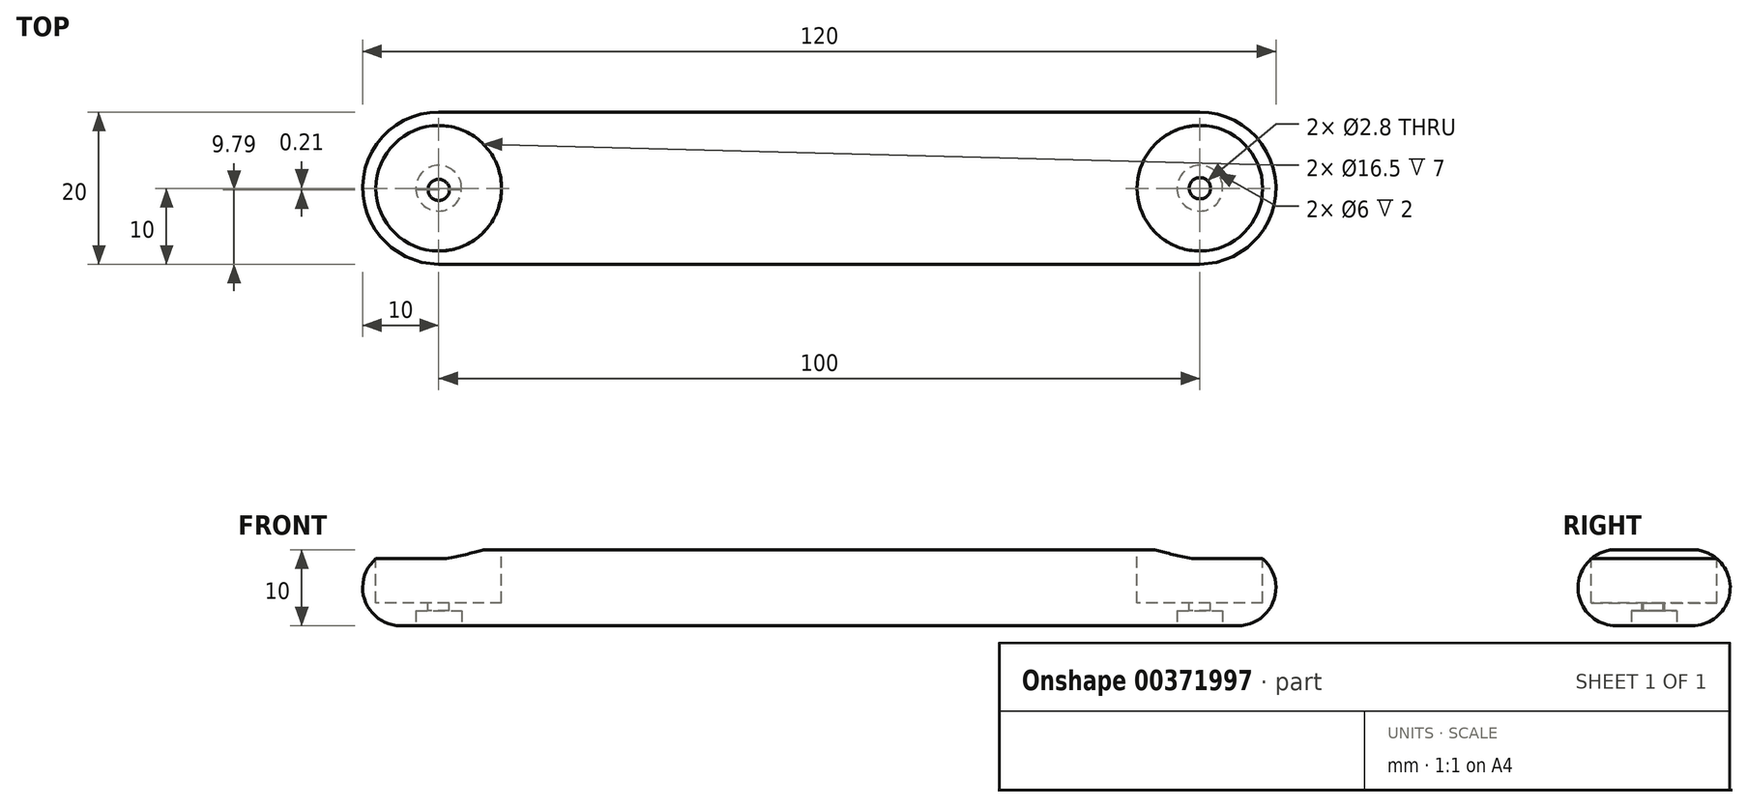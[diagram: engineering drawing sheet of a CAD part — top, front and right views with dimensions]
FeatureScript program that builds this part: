
annotation { "Feature Type Name" : "Feature", "Feature Type Description" : "" }
export const myFeature = defineFeature(function(context is Context, id is Id, definition is map)
    precondition{}
    {
        {
            var Q0;
            Q0=qCreatedBy(makeId("Top.planeOp"),FACE);
            var sketch = newSketch(context, id + "F0", { "sketchPlane" : qUnion([Q0])});
            skArc(sketch, "E0", {"start": v(0, 10) * mm, "mid": v(-10, 0) * mm, "end": v(0, -10) * mm});
            skArc(sketch, "E1", {"start": v(100, -10) * mm, "mid": v(110, 0) * mm, "end": v(100, 10) * mm});
            skLineSegment(sketch, "E2", {"start": v(0, 10) * mm, "end": v(100, 10) * mm});
            skLineSegment(sketch, "E3", {"start": v(0, -10) * mm, "end": v(100, -10) * mm});
            skSolve(sketch);
        }
        {
            var Q0;
            Q0=makeQuery(id+"F0.imprint","IMPRINT",FACE,{"disambiguationData":[TD([[makeQuery(id+"F0.imprint","IMPRINT",EDGE,{"derivedFrom":sQuery(id+"F0.wireOp",EDGE,"E0")}),1.0]])]});
            extrude(context, id + "F1", {"entities" : qUnion([Q0]), "depth" : 10 * mm});
        }
        {
            var Q0;
            Q0=makeQuery(id+"F1.opExtrude","CAP_FACE",FACE,{"disambiguationData":[OSD([sQuery(id+"F0.wireOp",EDGE,"E0"),sQuery(id+"F0.wireOp",EDGE,"E1"),sQuery(id+"F0.wireOp",EDGE,"E2"),sQuery(id+"F0.wireOp",EDGE,"E3")])],"isStart":false});
            var sketch = newSketch(context, id + "F2", { "sketchPlane" : qUnion([Q0])});
            skLineSegment(sketch, "E4.0.0", {"start": v(0, -10) * mm, "end": v(100, -10) * mm});
            skArc(sketch, "E4.0.1", {"start": v(100, -10) * mm, "mid": v(110, 0) * mm, "end": v(100, 10) * mm});
            skLineSegment(sketch, "E4.0.2", {"start": v(100, 10) * mm, "end": v(0, 10) * mm});
            skArc(sketch, "E4.0.3", {"start": v(0, 10) * mm, "mid": v(-10, 0) * mm, "end": v(0, -10) * mm});
            skCircle(sketch, "E5", {"center": v(0, 0) * mm, "radius": 8.25 * mm});
            skCircle(sketch, "E6", {"center": v(100, 0) * mm, "radius": 8.25 * mm});
            skSolve(sketch);
        }
        {
            var Q0;
            Q0=makeQuery(id+"F2.imprint","IMPRINT",FACE,{"disambiguationData":[TD([[makeQuery(id+"F2.imprint","IMPRINT",EDGE,{"derivedFrom":sQuery(id+"F2.wireOp",EDGE,"E5")}),1.0]])]});
            var Q1;
            Q1=makeQuery(id+"F2.imprint","IMPRINT",FACE,{"disambiguationData":[TD([[makeQuery(id+"F2.imprint","IMPRINT",EDGE,{"derivedFrom":sQuery(id+"F2.wireOp",EDGE,"E6")}),1.0]])]});
            extrude(context, id + "F3", {"entities" : qUnion([Q0, Q1]), "operationType" : NewBodyOperationType.REMOVE, "oppositeDirection" : true, "depth" : 7 * mm});
        }
        {
            var Q0;
            Q0=makeQuery(id+"F3.boolean.opBoolean","COPY",FACE,{"derivedFrom":makeQuery(id+"F3.opExtrude","CAP_FACE",FACE,{"disambiguationData":[OSD([sQuery(id+"F2.wireOp",EDGE,"E5")])],"isStart":false})});
            var sketch = newSketch(context, id + "F4", { "sketchPlane" : qUnion([Q0])});
            skCircle(sketch, "E7.0.0", {"center": v(100, 0) * mm, "radius": 8.25 * mm});
            skCircle(sketch, "E8.0.0", {"center": v(0, 0) * mm, "radius": 8.25 * mm});
            skCircle(sketch, "E9", {"center": v(0, -0.21) * mm, "radius": 1.4 * mm});
            skCircle(sketch, "E10", {"center": v(100, 0) * mm, "radius": 1.4 * mm});
            skSolve(sketch);
        }
        {
            var Q0;
            Q0=makeQuery(id+"F4.imprint","IMPRINT",FACE,{"disambiguationData":[TD([[makeQuery(id+"F4.imprint","IMPRINT",EDGE,{"derivedFrom":sQuery(id+"F4.wireOp",EDGE,"E9")}),1.0]])]});
            var Q1;
            Q1=makeQuery(id+"F4.imprint","IMPRINT",FACE,{"disambiguationData":[TD([[makeQuery(id+"F4.imprint","IMPRINT",EDGE,{"derivedFrom":sQuery(id+"F4.wireOp",EDGE,"E10")}),1.0]])]});
            extrude(context, id + "F5", {"entities" : qUnion([Q0, Q1]), "operationType" : NewBodyOperationType.REMOVE, "oppositeDirection" : true, "depth" : 25 * mm});
        }
        {
            var Q0;
            Q0=makeQuery(id+"F1.opExtrude","CAP_EDGE",EDGE,{"disambiguationData":[OSD([sQuery(id+"F0.wireOp",EDGE,"E2")])],"isStart":false});
            var Q1;
            Q1=makeQuery(id+"F1.opExtrude","CAP_EDGE",EDGE,{"disambiguationData":[OSD([sQuery(id+"F0.wireOp",EDGE,"E2")])],"isStart":true});
            fillet(context, id + "F6", {"entities" : qUnion([Q0, Q1]), "radius" : 5 * mm, "tangentPropagation" : true, "allowEdgeOverflow" : false});
        }
        {
            var Q0;
            Q0=makeQuery(id+"F1.opExtrude","CAP_FACE",FACE,{"disambiguationData":[OSD([sQuery(id+"F0.wireOp",EDGE,"E0"),sQuery(id+"F0.wireOp",EDGE,"E1"),sQuery(id+"F0.wireOp",EDGE,"E2"),sQuery(id+"F0.wireOp",EDGE,"E3")])],"isStart":true});
            var sketch = newSketch(context, id + "F7", { "sketchPlane" : qUnion([Q0])});
            skCircle(sketch, "E11", {"center": v(0, 0) * mm, "radius": 3 * mm});
            skCircle(sketch, "E12", {"center": v(100, 0) * mm, "radius": 3 * mm});
            skSolve(sketch);
        }
        {
            var Q0;
            Q0=makeQuery(id+"F7.imprint","IMPRINT",FACE,{"disambiguationData":[TD([[makeQuery(id+"F7.imprint","IMPRINT",EDGE,{"derivedFrom":sQuery(id+"F7.wireOp",EDGE,"E11")}),1.0]])]});
            var Q1;
            Q1=makeQuery(id+"F7.imprint","IMPRINT",FACE,{"disambiguationData":[TD([[makeQuery(id+"F7.imprint","IMPRINT",EDGE,{"derivedFrom":sQuery(id+"F7.wireOp",EDGE,"E12")}),1.0]])]});
            extrude(context, id + "F8", {"entities" : qUnion([Q0, Q1]), "operationType" : NewBodyOperationType.REMOVE, "oppositeDirection" : true, "depth" : 2 * mm});
        }
    });
